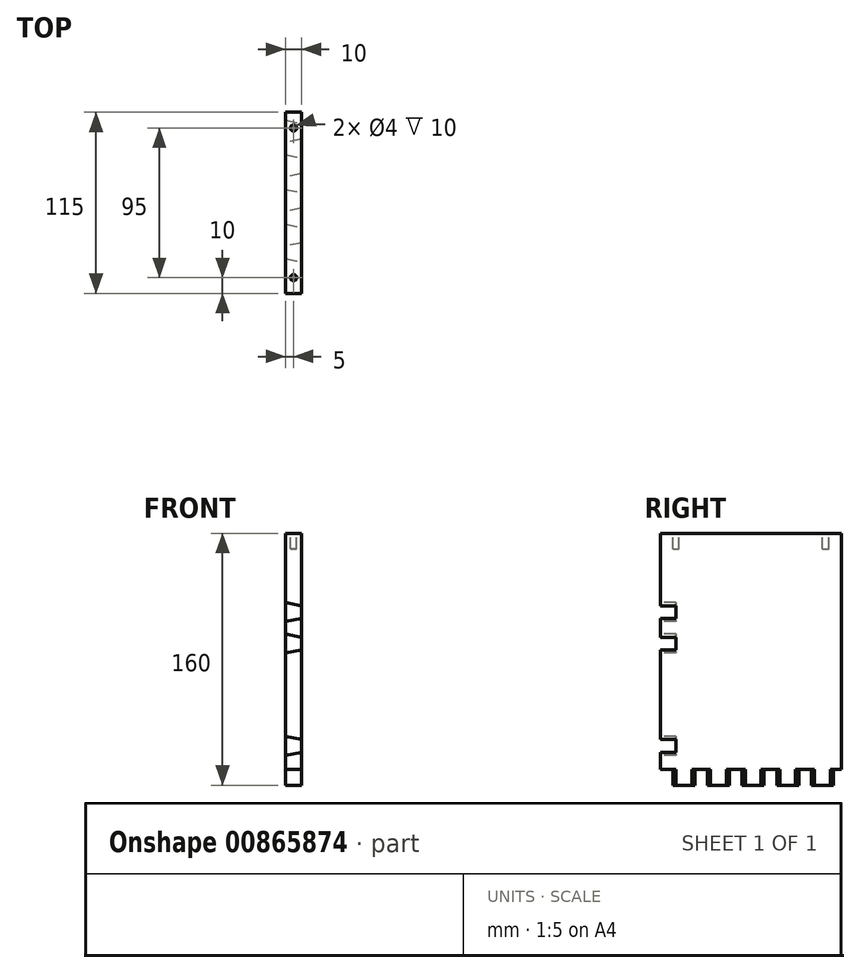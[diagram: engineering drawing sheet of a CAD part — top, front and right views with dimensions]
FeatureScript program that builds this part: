
annotation { "Feature Type Name" : "Feature", "Feature Type Description" : "" }
export const myFeature = defineFeature(function(context is Context, id is Id, definition is map)
    precondition{}
    {
        {
            var Q0;
            Q0=qCreatedBy(makeId("Right.planeOp"),FACE);
            var sketch = newSketch(context, id + "F0", { "sketchPlane" : qUnion([Q0])});
            skLineSegment(sketch, "E0.bottom", {"start": v(80, 87.53) * mm, "end": v(-35, 87.53) * mm});
            skLineSegment(sketch, "E0.left", {"start": v(80, 87.53) * mm, "end": v(80, -72.47) * mm});
            skLineSegment(sketch, "E0.right", {"start": v(-35, 87.53) * mm, "end": v(-35, -72.47) * mm});
            skLineSegment(sketch, "E1.trimOffspring", {"start": v(80, -72.47) * mm, "end": v(-35, -72.47) * mm});
            skSolve(sketch);
        }
        {
            var Q0;
            Q0 = qSketchRegion(id + "F0", true);
            extrude(context, id + "F1", {"entities" : qUnion([Q0]), "depth" : 10 * mm, "offsetDistance" : 25 * mm});
        }
        {
            var Q0;
            Q0=makeQuery(id+"F1.opExtrude","SWEPT_FACE",FACE,{"disambiguationData":[OSD([sQuery(id+"F0.wireOp",EDGE,"E0.right")])]});
            var sketch = newSketch(context, id + "F2", { "sketchPlane" : qUnion([Q0])});
            skLineSegment(sketch, "E2", {"start": v(0, 43.53) * mm, "end": v(0, 31.53) * mm});
            skLineSegment(sketch, "E3", {"start": v(0, 31.53) * mm, "end": v(10, 33.53) * mm});
            skLineSegment(sketch, "E4", {"start": v(10, 33.53) * mm, "end": v(10, 41.53) * mm});
            skLineSegment(sketch, "E5", {"start": v(10, 41.53) * mm, "end": v(0, 43.53) * mm});
            skLineSegment(sketch, "E6", {"start": v(0, 23.53) * mm, "end": v(0, 11.53) * mm});
            skLineSegment(sketch, "E7", {"start": v(0, 11.53) * mm, "end": v(10, 13.53) * mm});
            skLineSegment(sketch, "E8", {"start": v(10, 13.53) * mm, "end": v(10, 21.53) * mm});
            skLineSegment(sketch, "E9", {"start": v(10, 21.53) * mm, "end": v(0, 23.53) * mm});
            skLineSegment(sketch, "E10", {"start": v(0, -41.47) * mm, "end": v(0, -53.47) * mm});
            skLineSegment(sketch, "E11", {"start": v(0, -53.47) * mm, "end": v(10, -51.47) * mm});
            skLineSegment(sketch, "E12", {"start": v(10, -51.47) * mm, "end": v(10, -43.47) * mm});
            skLineSegment(sketch, "E13", {"start": v(10, -43.47) * mm, "end": v(0, -41.47) * mm});
            skSolve(sketch);
        }
        {
            var Q0;
            Q0 = qSketchRegion(id + "F2", true);
            extrude(context, id + "F3", {"entities" : qUnion([Q0]), "operationType" : NewBodyOperationType.REMOVE, "oppositeDirection" : true, "depth" : 10 * mm, "offsetDistance" : 25 * mm});
        }
        {
            var Q0;
            Q0=makeQuery(id+"F1.opExtrude","SWEPT_FACE",FACE,{"disambiguationData":[OSD([sQuery(id+"F0.wireOp",EDGE,"E1.trimOffspring")])]});
            var sketch = newSketch(context, id + "F4", { "sketchPlane" : qUnion([Q0])});
            skLineSegment(sketch, "E14", {"start": v(0, 35) * mm, "end": v(10, 37) * mm});
            skLineSegment(sketch, "E15", {"start": v(10, 37) * mm, "end": v(10, 25) * mm});
            skLineSegment(sketch, "E16", {"start": v(10, 25) * mm, "end": v(0, 27) * mm});
            skLineSegment(sketch, "E17", {"start": v(0, 27) * mm, "end": v(0, 35) * mm});
            skLineSegment(sketch, "E18.0.1.0", {"start": v(10, 15) * mm, "end": v(10, 3) * mm});
            skLineSegment(sketch, "E18.0.1.1", {"start": v(0, 13) * mm, "end": v(10, 15) * mm});
            skLineSegment(sketch, "E18.0.1.2", {"start": v(0, 5) * mm, "end": v(0, 13) * mm});
            skLineSegment(sketch, "E18.0.1.3", {"start": v(10, 3) * mm, "end": v(0, 5) * mm});
            skLineSegment(sketch, "E18.0.2.0", {"start": v(10, -7) * mm, "end": v(10, -19) * mm});
            skLineSegment(sketch, "E18.0.2.1", {"start": v(0, -9) * mm, "end": v(10, -7) * mm});
            skLineSegment(sketch, "E18.0.2.2", {"start": v(0, -17) * mm, "end": v(0, -9) * mm});
            skLineSegment(sketch, "E18.0.2.3", {"start": v(10, -19) * mm, "end": v(0, -17) * mm});
            skLineSegment(sketch, "E18.0.3.0", {"start": v(10, -29) * mm, "end": v(10, -41) * mm});
            skLineSegment(sketch, "E18.0.3.1", {"start": v(0, -31) * mm, "end": v(10, -29) * mm});
            skLineSegment(sketch, "E18.0.3.2", {"start": v(0, -39) * mm, "end": v(0, -31) * mm});
            skLineSegment(sketch, "E18.0.3.3", {"start": v(10, -41) * mm, "end": v(0, -39) * mm});
            skLineSegment(sketch, "E18.0.4.0", {"start": v(10, -51) * mm, "end": v(10, -63) * mm});
            skLineSegment(sketch, "E18.0.4.1", {"start": v(0, -53) * mm, "end": v(10, -51) * mm});
            skLineSegment(sketch, "E18.0.4.2", {"start": v(0, -61) * mm, "end": v(0, -53) * mm});
            skLineSegment(sketch, "E18.0.4.3", {"start": v(10, -63) * mm, "end": v(0, -61) * mm});
            skLineSegment(sketch, "E18.direction1", {"start": v(0, 27) * mm, "end": v(25, 27) * mm, "construction": true});
            skLineSegment(sketch, "E18.direction2", {"start": v(0, 27) * mm, "end": v(0, 5) * mm, "construction": true});
            skLineSegment(sketch, "E19.0.0.5", {"start": v(10, -73) * mm, "end": v(10, -85) * mm});
            skLineSegment(sketch, "E19.3.0.5", {"start": v(0, -75) * mm, "end": v(10, -73) * mm});
            skLineSegment(sketch, "E19.6.0.5", {"start": v(0, -83) * mm, "end": v(0, -75) * mm});
            skLineSegment(sketch, "E19.9.0.5", {"start": v(10, -85) * mm, "end": v(0, -83) * mm});
            skSolve(sketch);
        }
        {
            var Q0;
            Q0 = qSketchRegion(id + "F4", true);
            extrude(context, id + "F5", {"entities" : qUnion([Q0]), "operationType" : NewBodyOperationType.REMOVE, "oppositeDirection" : true, "depth" : 10 * mm, "offsetDistance" : 25 * mm});
        }
        {
            var Q0;
            Q0=makeQuery(id+"F1.opExtrude","SWEPT_FACE",FACE,{"disambiguationData":[OSD([sQuery(id+"F0.wireOp",EDGE,"E0.bottom")])]});
            var sketch = newSketch(context, id + "F6", { "sketchPlane" : qUnion([Q0])});
            skCircle(sketch, "E20", {"center": v(5, 70) * mm, "radius": 2 * mm});
            skPoint(sketch, "E20.centerSnap0", {"position": v(5, 80) * mm});
            skCircle(sketch, "E21", {"center": v(5, -25) * mm, "radius": 2 * mm});
            skPoint(sketch, "E21.centerSnap0", {"position": v(5, -35) * mm});
            skSolve(sketch);
        }
        {
            var Q0;
            Q0 = qSketchRegion(id + "F6", true);
            extrude(context, id + "F7", {"entities" : qUnion([Q0]), "operationType" : NewBodyOperationType.REMOVE, "oppositeDirection" : true, "depth" : 10 * mm, "offsetDistance" : 25 * mm});
        }
    });
